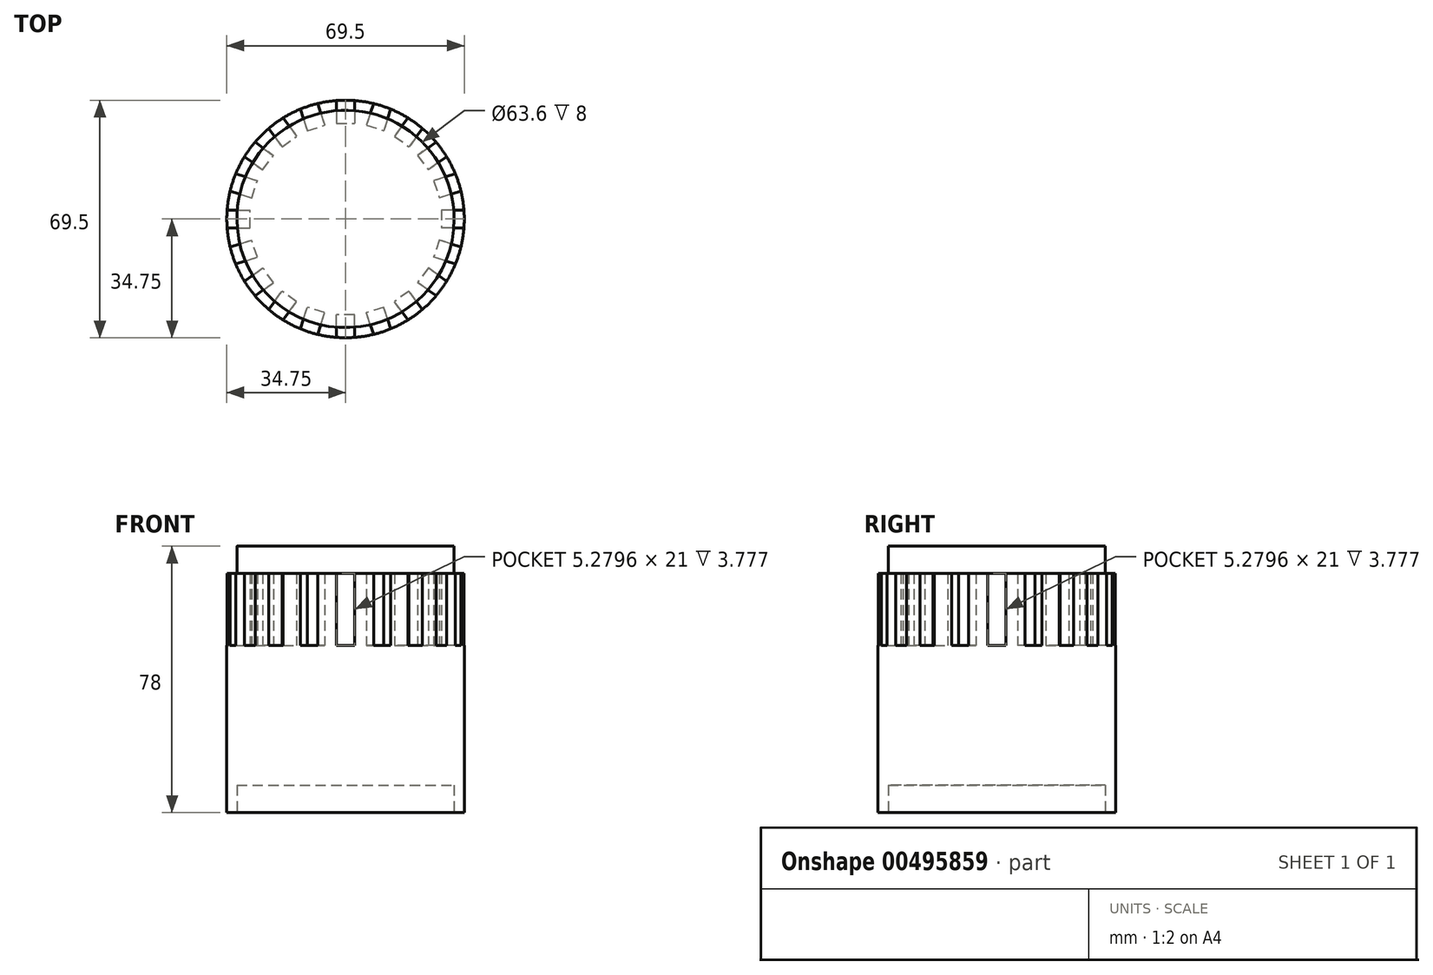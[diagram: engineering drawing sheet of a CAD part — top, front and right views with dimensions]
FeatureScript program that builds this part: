
annotation { "Feature Type Name" : "Feature", "Feature Type Description" : "" }
export const myFeature = defineFeature(function(context is Context, id is Id, definition is map)
    precondition{}
    {
        {
            var Q0;
            Q0=qCreatedBy(makeId("Top.planeOp"),FACE);
            var sketch = newSketch(context, id + "F0", { "sketchPlane" : qUnion([Q0])});
            skCircle(sketch, "E0", {"center": v(0, 0) * mm, "radius": 34.75 * mm});
            skSolve(sketch);
        }
        {
            var Q0;
            Q0=qSketchRegion(id+"F0",true);
            extrude(context, id + "F1", {"entities" : qUnion([Q0]), "depth" : (61 - 12) * mm});
        }
        {
            var Q0;
            Q0=makeQuery(id+"F1.opExtrude","CAP_FACE",FACE,{"disambiguationData":[OSD([sQuery(id+"F0.wireOp",EDGE,"E0")])],"isStart":false});
            var sketch = newSketch(context, id + "F2", { "sketchPlane" : qUnion([Q0])});
            skArc(sketch, "E1.0", {"start": v(-2.64, 34.65) * mm, "mid": v(-5.44, 34.32) * mm, "end": v(-8.2, 33.77) * mm});
            skLineSegment(sketch, "E2.top", {"start": v(-2.64, 28.01) * mm, "end": v(2.64, 28.01) * mm});
            skLineSegment(sketch, "E2.left", {"start": v(-2.64, 34.65) * mm, "end": v(-2.64, 28.01) * mm});
            skLineSegment(sketch, "E2.right", {"start": v(2.64, 34.65) * mm, "end": v(2.64, 28.01) * mm});
            skLineSegment(sketch, "E3.1.0", {"start": v(-13.22, 32.14) * mm, "end": v(-11.17, 25.82) * mm});
            skLineSegment(sketch, "E3.1.1", {"start": v(-11.17, 25.82) * mm, "end": v(-6.15, 27.46) * mm});
            skLineSegment(sketch, "E3.1.2", {"start": v(-8.2, 33.77) * mm, "end": v(-6.15, 27.46) * mm});
            skLineSegment(sketch, "E3.2.0", {"start": v(-22.5, 26.48) * mm, "end": v(-18.6, 21.1) * mm});
            skLineSegment(sketch, "E3.2.1", {"start": v(-18.6, 21.1) * mm, "end": v(-14.33, 24.21) * mm});
            skLineSegment(sketch, "E3.2.2", {"start": v(-18.23, 29.58) * mm, "end": v(-14.33, 24.21) * mm});
            skLineSegment(sketch, "E3.3.0", {"start": v(-29.58, 18.23) * mm, "end": v(-24.21, 14.33) * mm});
            skLineSegment(sketch, "E3.3.1", {"start": v(-24.21, 14.33) * mm, "end": v(-21.1, 18.6) * mm});
            skLineSegment(sketch, "E3.3.2", {"start": v(-26.48, 22.5) * mm, "end": v(-21.1, 18.6) * mm});
            skLineSegment(sketch, "E3.4.0", {"start": v(-33.77, 8.2) * mm, "end": v(-27.46, 6.15) * mm});
            skLineSegment(sketch, "E3.4.1", {"start": v(-27.46, 6.15) * mm, "end": v(-25.82, 11.17) * mm});
            skLineSegment(sketch, "E3.4.2", {"start": v(-32.14, 13.22) * mm, "end": v(-25.82, 11.17) * mm});
            skLineSegment(sketch, "E3.5.0", {"start": v(-34.65, -2.64) * mm, "end": v(-28.01, -2.64) * mm});
            skLineSegment(sketch, "E3.5.1", {"start": v(-28.01, -2.64) * mm, "end": v(-28.01, 2.64) * mm});
            skLineSegment(sketch, "E3.5.2", {"start": v(-34.65, 2.64) * mm, "end": v(-28.01, 2.64) * mm});
            skLineSegment(sketch, "E3.6.0", {"start": v(-32.14, -13.22) * mm, "end": v(-25.82, -11.17) * mm});
            skLineSegment(sketch, "E3.6.1", {"start": v(-25.82, -11.17) * mm, "end": v(-27.46, -6.15) * mm});
            skLineSegment(sketch, "E3.6.2", {"start": v(-33.77, -8.2) * mm, "end": v(-27.46, -6.15) * mm});
            skLineSegment(sketch, "E3.7.0", {"start": v(-26.48, -22.5) * mm, "end": v(-21.1, -18.6) * mm});
            skLineSegment(sketch, "E3.7.1", {"start": v(-21.1, -18.6) * mm, "end": v(-24.21, -14.33) * mm});
            skLineSegment(sketch, "E3.7.2", {"start": v(-29.58, -18.23) * mm, "end": v(-24.21, -14.33) * mm});
            skLineSegment(sketch, "E3.8.0", {"start": v(-18.23, -29.58) * mm, "end": v(-14.33, -24.21) * mm});
            skLineSegment(sketch, "E3.8.1", {"start": v(-14.33, -24.21) * mm, "end": v(-18.6, -21.1) * mm});
            skLineSegment(sketch, "E3.8.2", {"start": v(-22.5, -26.48) * mm, "end": v(-18.6, -21.1) * mm});
            skLineSegment(sketch, "E3.9.0", {"start": v(-8.2, -33.77) * mm, "end": v(-6.15, -27.46) * mm});
            skLineSegment(sketch, "E3.9.1", {"start": v(-6.15, -27.46) * mm, "end": v(-11.17, -25.82) * mm});
            skLineSegment(sketch, "E3.9.2", {"start": v(-13.22, -32.14) * mm, "end": v(-11.17, -25.82) * mm});
            skLineSegment(sketch, "E3.10.0", {"start": v(2.64, -34.65) * mm, "end": v(2.64, -28.01) * mm});
            skLineSegment(sketch, "E3.10.1", {"start": v(2.64, -28.01) * mm, "end": v(-2.64, -28.01) * mm});
            skLineSegment(sketch, "E3.10.2", {"start": v(-2.64, -34.65) * mm, "end": v(-2.64, -28.01) * mm});
            skLineSegment(sketch, "E3.11.0", {"start": v(13.22, -32.14) * mm, "end": v(11.17, -25.82) * mm});
            skLineSegment(sketch, "E3.11.1", {"start": v(11.17, -25.82) * mm, "end": v(6.15, -27.46) * mm});
            skLineSegment(sketch, "E3.11.2", {"start": v(8.2, -33.77) * mm, "end": v(6.15, -27.46) * mm});
            skLineSegment(sketch, "E3.12.0", {"start": v(22.5, -26.48) * mm, "end": v(18.6, -21.1) * mm});
            skLineSegment(sketch, "E3.12.1", {"start": v(18.6, -21.1) * mm, "end": v(14.33, -24.21) * mm});
            skLineSegment(sketch, "E3.12.2", {"start": v(18.23, -29.58) * mm, "end": v(14.33, -24.21) * mm});
            skLineSegment(sketch, "E3.13.0", {"start": v(29.58, -18.23) * mm, "end": v(24.21, -14.33) * mm});
            skLineSegment(sketch, "E3.13.1", {"start": v(24.21, -14.33) * mm, "end": v(21.1, -18.6) * mm});
            skLineSegment(sketch, "E3.13.2", {"start": v(26.48, -22.5) * mm, "end": v(21.1, -18.6) * mm});
            skLineSegment(sketch, "E3.14.0", {"start": v(33.77, -8.2) * mm, "end": v(27.46, -6.15) * mm});
            skLineSegment(sketch, "E3.14.1", {"start": v(27.46, -6.15) * mm, "end": v(25.82, -11.17) * mm});
            skLineSegment(sketch, "E3.14.2", {"start": v(32.14, -13.22) * mm, "end": v(25.82, -11.17) * mm});
            skLineSegment(sketch, "E3.15.0", {"start": v(34.65, 2.64) * mm, "end": v(28.01, 2.64) * mm});
            skLineSegment(sketch, "E3.15.1", {"start": v(28.01, 2.64) * mm, "end": v(28.01, -2.64) * mm});
            skLineSegment(sketch, "E3.15.2", {"start": v(34.65, -2.64) * mm, "end": v(28.01, -2.64) * mm});
            skLineSegment(sketch, "E3.16.0", {"start": v(32.14, 13.22) * mm, "end": v(25.82, 11.17) * mm});
            skLineSegment(sketch, "E3.16.1", {"start": v(25.82, 11.17) * mm, "end": v(27.46, 6.15) * mm});
            skLineSegment(sketch, "E3.16.2", {"start": v(33.77, 8.2) * mm, "end": v(27.46, 6.15) * mm});
            skLineSegment(sketch, "E3.17.0", {"start": v(26.48, 22.5) * mm, "end": v(21.1, 18.6) * mm});
            skLineSegment(sketch, "E3.17.1", {"start": v(21.1, 18.6) * mm, "end": v(24.21, 14.33) * mm});
            skLineSegment(sketch, "E3.17.2", {"start": v(29.58, 18.23) * mm, "end": v(24.21, 14.33) * mm});
            skLineSegment(sketch, "E3.18.0", {"start": v(18.23, 29.58) * mm, "end": v(14.33, 24.21) * mm});
            skLineSegment(sketch, "E3.18.1", {"start": v(14.33, 24.21) * mm, "end": v(18.6, 21.1) * mm});
            skLineSegment(sketch, "E3.18.2", {"start": v(22.5, 26.48) * mm, "end": v(18.6, 21.1) * mm});
            skLineSegment(sketch, "E3.19.0", {"start": v(8.2, 33.77) * mm, "end": v(6.15, 27.46) * mm});
            skLineSegment(sketch, "E3.19.1", {"start": v(6.15, 27.46) * mm, "end": v(11.17, 25.82) * mm});
            skLineSegment(sketch, "E3.19.2", {"start": v(13.22, 32.14) * mm, "end": v(11.17, 25.82) * mm});
            skArc(sketch, "E4.trimOffspring", {"start": v(-13.22, 32.14) * mm, "mid": v(-15.78, 30.96) * mm, "end": v(-18.23, 29.58) * mm});
            skArc(sketch, "E5.trimOffspring", {"start": v(-22.5, 26.48) * mm, "mid": v(-24.57, 24.57) * mm, "end": v(-26.48, 22.5) * mm});
            skArc(sketch, "E6.trimOffspring", {"start": v(-29.58, 18.23) * mm, "mid": v(-30.96, 15.78) * mm, "end": v(-32.14, 13.22) * mm});
            skArc(sketch, "E7.trimOffspring", {"start": v(-33.77, 8.2) * mm, "mid": v(-34.32, 5.44) * mm, "end": v(-34.65, 2.64) * mm});
            skArc(sketch, "E8.trimOffspring", {"start": v(-34.65, -2.64) * mm, "mid": v(-34.32, -5.44) * mm, "end": v(-33.77, -8.2) * mm});
            skArc(sketch, "E9.trimOffspring", {"start": v(-32.14, -13.22) * mm, "mid": v(-30.96, -15.78) * mm, "end": v(-29.58, -18.23) * mm});
            skArc(sketch, "E10.trimOffspring", {"start": v(-26.48, -22.5) * mm, "mid": v(-24.57, -24.57) * mm, "end": v(-22.5, -26.48) * mm});
            skArc(sketch, "E11.trimOffspring", {"start": v(-18.23, -29.58) * mm, "mid": v(-15.78, -30.96) * mm, "end": v(-13.22, -32.14) * mm});
            skArc(sketch, "E12.trimOffspring", {"start": v(-8.2, -33.77) * mm, "mid": v(-5.44, -34.32) * mm, "end": v(-2.64, -34.65) * mm});
            skArc(sketch, "E13.trimOffspring", {"start": v(2.64, -34.65) * mm, "mid": v(5.44, -34.32) * mm, "end": v(8.2, -33.77) * mm});
            skArc(sketch, "E14.trimOffspring", {"start": v(13.22, -32.14) * mm, "mid": v(15.78, -30.96) * mm, "end": v(18.23, -29.58) * mm});
            skArc(sketch, "E15.trimOffspring", {"start": v(22.5, -26.48) * mm, "mid": v(24.57, -24.57) * mm, "end": v(26.48, -22.5) * mm});
            skArc(sketch, "E16.trimOffspring", {"start": v(29.58, -18.23) * mm, "mid": v(30.96, -15.78) * mm, "end": v(32.14, -13.22) * mm});
            skArc(sketch, "E17.trimOffspring", {"start": v(33.77, -8.2) * mm, "mid": v(34.32, -5.44) * mm, "end": v(34.65, -2.64) * mm});
            skArc(sketch, "E18.trimOffspring", {"start": v(34.65, 2.64) * mm, "mid": v(34.32, 5.44) * mm, "end": v(33.77, 8.2) * mm});
            skArc(sketch, "E19.trimOffspring", {"start": v(32.14, 13.22) * mm, "mid": v(30.96, 15.78) * mm, "end": v(29.58, 18.23) * mm});
            skArc(sketch, "E20.trimOffspring", {"start": v(26.48, 22.5) * mm, "mid": v(24.57, 24.57) * mm, "end": v(22.5, 26.48) * mm});
            skArc(sketch, "E21.trimOffspring", {"start": v(18.23, 29.58) * mm, "mid": v(15.78, 30.96) * mm, "end": v(13.22, 32.14) * mm});
            skArc(sketch, "E22.trimOffspring", {"start": v(8.2, 33.77) * mm, "mid": v(5.44, 34.32) * mm, "end": v(2.64, 34.65) * mm});
            skSolve(sketch);
        }
        {
            var Q0;
            Q0=qSketchRegion(id+"F2",true);
            extrude(context, id + "F3", {"entities" : qUnion([Q0]), "operationType" : NewBodyOperationType.ADD, "depth" : 21 * mm});
        }
        {
            var Q0;
            Q0=makeQuery(id+"F3.opExtrude","CAP_FACE",FACE,{"disambiguationData":[OSD([sQuery(id+"F2.wireOp",EDGE,"E1.0"),sQuery(id+"F2.wireOp",EDGE,"E2.top"),sQuery(id+"F2.wireOp",EDGE,"E2.left"),sQuery(id+"F2.wireOp",EDGE,"E2.right"),sQuery(id+"F2.wireOp",EDGE,"E3.1.0"),sQuery(id+"F2.wireOp",EDGE,"E3.1.1"),sQuery(id+"F2.wireOp",EDGE,"E3.1.2"),sQuery(id+"F2.wireOp",EDGE,"E3.2.0"),sQuery(id+"F2.wireOp",EDGE,"E3.2.1"),sQuery(id+"F2.wireOp",EDGE,"E3.2.2"),sQuery(id+"F2.wireOp",EDGE,"E3.3.0"),sQuery(id+"F2.wireOp",EDGE,"E3.3.1"),sQuery(id+"F2.wireOp",EDGE,"E3.3.2"),sQuery(id+"F2.wireOp",EDGE,"E3.4.0"),sQuery(id+"F2.wireOp",EDGE,"E3.4.1"),sQuery(id+"F2.wireOp",EDGE,"E3.4.2"),sQuery(id+"F2.wireOp",EDGE,"E3.5.0"),sQuery(id+"F2.wireOp",EDGE,"E3.5.1"),sQuery(id+"F2.wireOp",EDGE,"E3.5.2"),sQuery(id+"F2.wireOp",EDGE,"E3.6.0"),sQuery(id+"F2.wireOp",EDGE,"E3.6.1"),sQuery(id+"F2.wireOp",EDGE,"E3.6.2"),sQuery(id+"F2.wireOp",EDGE,"E3.7.0"),sQuery(id+"F2.wireOp",EDGE,"E3.7.1"),sQuery(id+"F2.wireOp",EDGE,"E3.7.2"),sQuery(id+"F2.wireOp",EDGE,"E3.8.0"),sQuery(id+"F2.wireOp",EDGE,"E3.8.1"),sQuery(id+"F2.wireOp",EDGE,"E3.8.2"),sQuery(id+"F2.wireOp",EDGE,"E3.9.0"),sQuery(id+"F2.wireOp",EDGE,"E3.9.1"),sQuery(id+"F2.wireOp",EDGE,"E3.9.2"),sQuery(id+"F2.wireOp",EDGE,"E3.10.0"),sQuery(id+"F2.wireOp",EDGE,"E3.10.1"),sQuery(id+"F2.wireOp",EDGE,"E3.10.2"),sQuery(id+"F2.wireOp",EDGE,"E3.11.0"),sQuery(id+"F2.wireOp",EDGE,"E3.11.1"),sQuery(id+"F2.wireOp",EDGE,"E3.11.2"),sQuery(id+"F2.wireOp",EDGE,"E3.12.0"),sQuery(id+"F2.wireOp",EDGE,"E3.12.1"),sQuery(id+"F2.wireOp",EDGE,"E3.12.2"),sQuery(id+"F2.wireOp",EDGE,"E3.13.0"),sQuery(id+"F2.wireOp",EDGE,"E3.13.1"),sQuery(id+"F2.wireOp",EDGE,"E3.13.2"),sQuery(id+"F2.wireOp",EDGE,"E3.14.0"),sQuery(id+"F2.wireOp",EDGE,"E3.14.1"),sQuery(id+"F2.wireOp",EDGE,"E3.14.2"),sQuery(id+"F2.wireOp",EDGE,"E3.15.0"),sQuery(id+"F2.wireOp",EDGE,"E3.15.1"),sQuery(id+"F2.wireOp",EDGE,"E3.15.2"),sQuery(id+"F2.wireOp",EDGE,"E3.16.0"),sQuery(id+"F2.wireOp",EDGE,"E3.16.1"),sQuery(id+"F2.wireOp",EDGE,"E3.16.2"),sQuery(id+"F2.wireOp",EDGE,"E3.17.0"),sQuery(id+"F2.wireOp",EDGE,"E3.17.1"),sQuery(id+"F2.wireOp",EDGE,"E3.17.2"),sQuery(id+"F2.wireOp",EDGE,"E3.18.0"),sQuery(id+"F2.wireOp",EDGE,"E3.18.1"),sQuery(id+"F2.wireOp",EDGE,"E3.18.2"),sQuery(id+"F2.wireOp",EDGE,"E3.19.0"),sQuery(id+"F2.wireOp",EDGE,"E3.19.1"),sQuery(id+"F2.wireOp",EDGE,"E3.19.2"),sQuery(id+"F2.wireOp",EDGE,"E4.trimOffspring"),sQuery(id+"F2.wireOp",EDGE,"E5.trimOffspring"),sQuery(id+"F2.wireOp",EDGE,"E6.trimOffspring"),sQuery(id+"F2.wireOp",EDGE,"E7.trimOffspring"),sQuery(id+"F2.wireOp",EDGE,"E8.trimOffspring"),sQuery(id+"F2.wireOp",EDGE,"E9.trimOffspring"),sQuery(id+"F2.wireOp",EDGE,"E10.trimOffspring"),sQuery(id+"F2.wireOp",EDGE,"E11.trimOffspring"),sQuery(id+"F2.wireOp",EDGE,"E12.trimOffspring"),sQuery(id+"F2.wireOp",EDGE,"E13.trimOffspring"),sQuery(id+"F2.wireOp",EDGE,"E14.trimOffspring"),sQuery(id+"F2.wireOp",EDGE,"E15.trimOffspring"),sQuery(id+"F2.wireOp",EDGE,"E16.trimOffspring"),sQuery(id+"F2.wireOp",EDGE,"E17.trimOffspring"),sQuery(id+"F2.wireOp",EDGE,"E18.trimOffspring"),sQuery(id+"F2.wireOp",EDGE,"E19.trimOffspring"),sQuery(id+"F2.wireOp",EDGE,"E20.trimOffspring"),sQuery(id+"F2.wireOp",EDGE,"E21.trimOffspring"),sQuery(id+"F2.wireOp",EDGE,"E22.trimOffspring")])],"isStart":false});
            var sketch = newSketch(context, id + "F4", { "sketchPlane" : qUnion([Q0])});
            skCircle(sketch, "E23", {"center": v(0, 0) * mm, "radius": 31.8 * mm});
            skSolve(sketch);
        }
        {
            var Q0;
            Q0=qSketchRegion(id+"F4",true);
            extrude(context, id + "F5", {"entities" : qUnion([Q0]), "operationType" : NewBodyOperationType.ADD, "depth" : 8 * mm});
        }
        {
            var Q0;
            Q0=makeQuery(id+"F1.opExtrude","CAP_FACE",FACE,{"disambiguationData":[OSD([sQuery(id+"F0.wireOp",EDGE,"E0")])],"isStart":true});
            var sketch = newSketch(context, id + "F6", { "sketchPlane" : qUnion([Q0])});
            skCircle(sketch, "E24", {"center": v(0, 0) * mm, "radius": 31.8 * mm});
            skSolve(sketch);
        }
        {
            var Q0;
            Q0=qSketchRegion(id+"F6",true);
            extrude(context, id + "F7", {"entities" : qUnion([Q0]), "operationType" : NewBodyOperationType.REMOVE, "oppositeDirection" : true, "depth" : 8 * mm});
        }
    });
